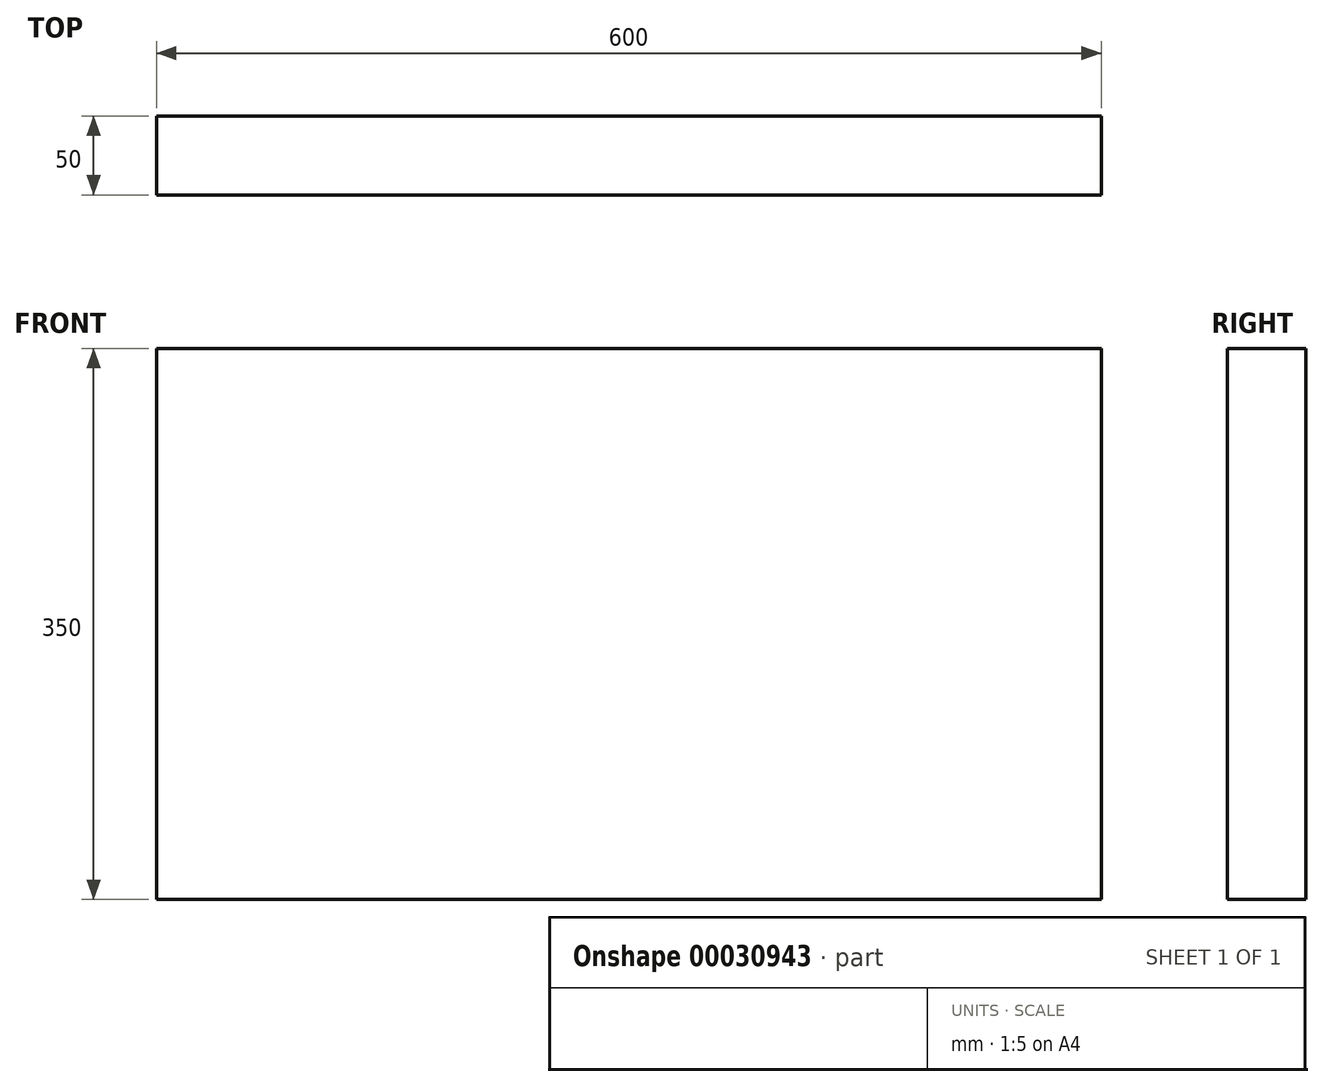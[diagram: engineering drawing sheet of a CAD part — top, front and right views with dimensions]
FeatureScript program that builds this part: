
annotation { "Feature Type Name" : "Feature", "Feature Type Description" : "" }
export const myFeature = defineFeature(function(context is Context, id is Id, definition is map)
    precondition{}
    {
        {
            var Q0;
            Q0=qCreatedBy(makeId("Right.planeOp"),FACE);
            var sketch = newSketch(context, id + "F0", { "sketchPlane" : qUnion([Q0])});
            skLineSegment(sketch, "E0.bottom", {"start": v(0, 555) * mm, "end": v(50, 555) * mm});
            skLineSegment(sketch, "E0.top", {"start": v(0, 205) * mm, "end": v(50, 205) * mm});
            skLineSegment(sketch, "E0.left", {"start": v(0, 555) * mm, "end": v(0, 205) * mm});
            skLineSegment(sketch, "E0.right", {"start": v(50, 555) * mm, "end": v(50, 205) * mm});
            skSolve(sketch);
        }
        {
            var Q0;
            Q0 = qSketchRegion(id + "F0", true);
            extrude(context, id + "F1", {"entities" : qUnion([Q0]), "depth" : 600 * mm});
        }
    });
